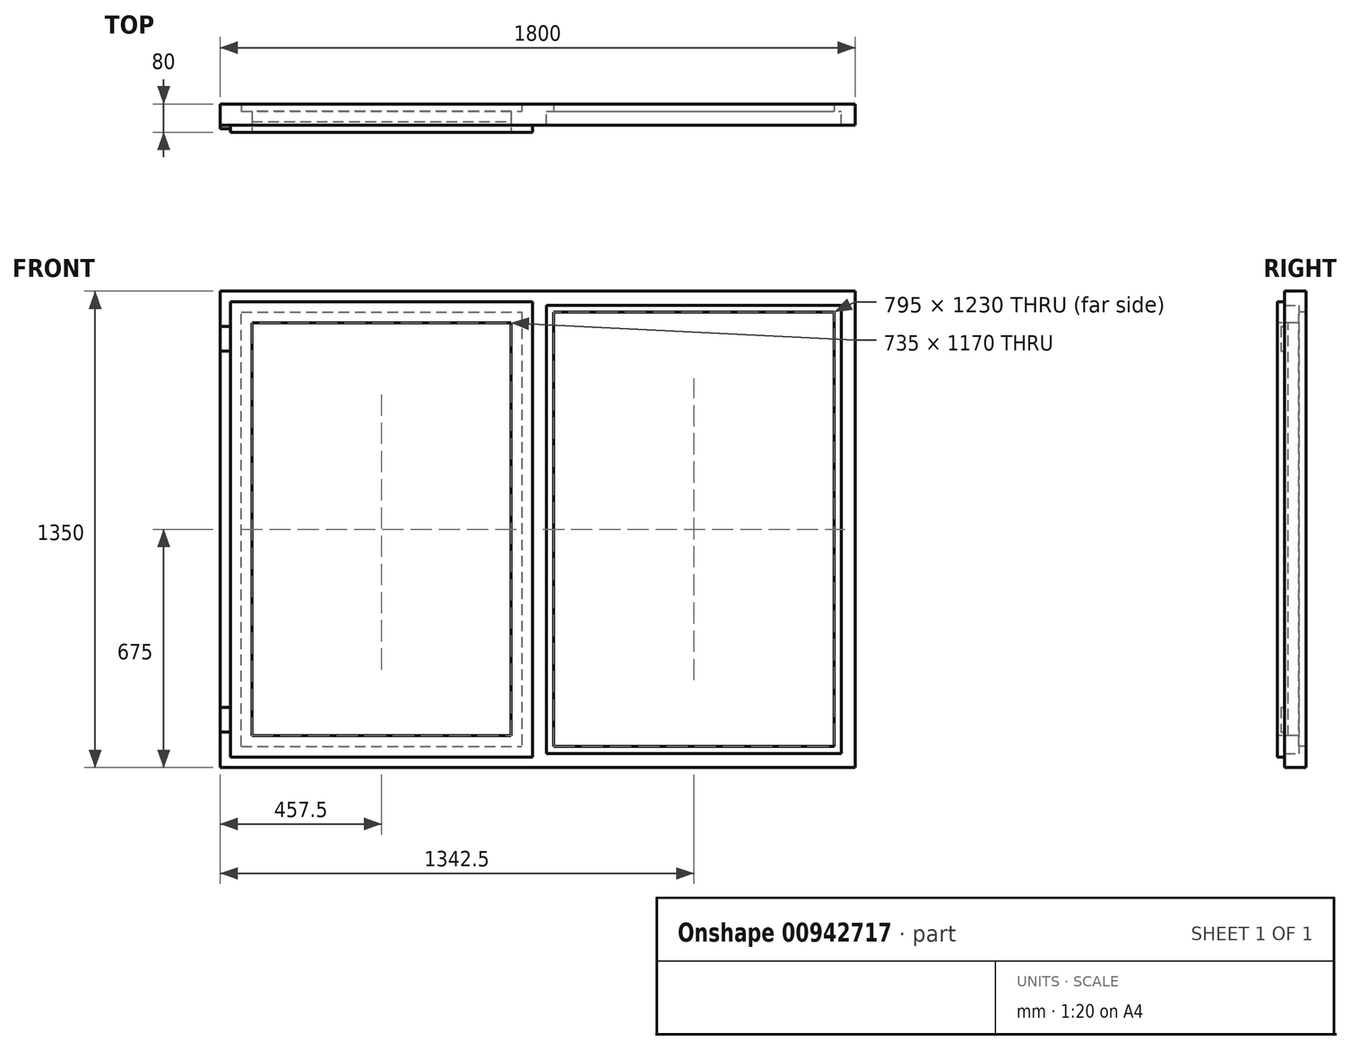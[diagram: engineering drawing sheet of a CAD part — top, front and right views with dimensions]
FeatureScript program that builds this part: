
annotation { "Feature Type Name" : "Feature", "Feature Type Description" : "" }
export const myFeature = defineFeature(function(context is Context, id is Id, definition is map)
    precondition{}
    {
        {
            var Q0;
            Q0=qCreatedBy(makeId("Front.planeOp"),FACE);
            var sketch = newSketch(context, id + "F0", { "sketchPlane" : qUnion([Q0])});
            skLineSegment(sketch, "E0.bottom", {"start": v(900, 675) * mm, "end": v(-900, 675) * mm});
            skLineSegment(sketch, "E0.top", {"start": v(900, -675) * mm, "end": v(-900, -675) * mm});
            skLineSegment(sketch, "E0.left", {"start": v(900, 675) * mm, "end": v(900, -675) * mm});
            skLineSegment(sketch, "E0.right", {"start": v(-900, 675) * mm, "end": v(-900, -675) * mm});
            skLineSegment(sketch, "E1", {"start": v(0, 675) * mm, "end": v(0, 0) * mm, "construction": true});
            skLineSegment(sketch, "E2", {"start": v(900, 0) * mm, "end": v(0, 0) * mm, "construction": true});
            skLineSegment(sketch, "E3", {"start": v(0, 0) * mm, "end": v(-900, 0) * mm, "construction": true});
            skLineSegment(sketch, "E4.bottom", {"start": v(-860, 635) * mm, "end": v(860, 635) * mm});
            skLineSegment(sketch, "E4.top", {"start": v(-860, -635) * mm, "end": v(860, -635) * mm});
            skLineSegment(sketch, "E4.left", {"start": v(-860, 635) * mm, "end": v(-860, -635) * mm});
            skLineSegment(sketch, "E4.right", {"start": v(860, 635) * mm, "end": v(860, -635) * mm});
            skLineSegment(sketch, "E5", {"start": v(0, 0) * mm, "end": v(0, -635) * mm, "construction": true});
            skLineSegment(sketch, "E6", {"start": v(0, 635) * mm, "end": v(0, -635) * mm, "construction": true});
            skLineSegment(sketch, "E7.bottom", {"start": v(-840, -615) * mm, "end": v(840, -615) * mm});
            skLineSegment(sketch, "E7.top", {"start": v(-840, 615) * mm, "end": v(840, 615) * mm});
            skLineSegment(sketch, "E7.left", {"start": v(-840, -615) * mm, "end": v(-840, 615) * mm});
            skLineSegment(sketch, "E7.right", {"start": v(840, -615) * mm, "end": v(840, 615) * mm});
            skLineSegment(sketch, "E8", {"start": v(-25, 635) * mm, "end": v(-25, -635) * mm});
            skLineSegment(sketch, "E9", {"start": v(25, -635) * mm, "end": v(25, 635) * mm});
            skLineSegment(sketch, "E10", {"start": v(-45, 615) * mm, "end": v(-45, -615) * mm});
            skLineSegment(sketch, "E11", {"start": v(45, -615) * mm, "end": v(45, 615) * mm});
            skSolve(sketch);
        }
        {
            var Q0;
            Q0=makeQuery(id+"F0.imprint","IMPRINT",FACE,{"disambiguationData":[TD([[makeQuery(id+"F0.imprint","IMPRINT",EDGE,{"derivedFrom":sQuery(id+"F0.wireOp",EDGE,"E0.bottom")}),1.0]])]});
            extrude(context, id + "F1", {"entities" : qUnion([Q0]), "depth" : 40 * mm, "offsetDistance" : 25 * mm});
        }
        {
            var Q0;
            {var subQ0=sQuery(id+"F0.wireOp",EDGE,"E4.left");Q0=makeQuery(id+"F0.imprint","IMPRINT",FACE,{"disambiguationData":[TD([[makeQuery(id+"F0.imprint","IMPRINT",EDGE,{"derivedFrom":subQ0}),1.0]])]});}
            var Q1;
            {var subQ8=sQuery(id+"F0.wireOp",EDGE,"E4.right");Q1=makeQuery(id+"F0.imprint","IMPRINT",FACE,{"disambiguationData":[TD([[makeQuery(id+"F0.imprint","IMPRINT",EDGE,{"derivedFrom":subQ8}),-1.0]])]});}
            var Q2;
            {var subQ0=sQuery(id+"F0.wireOp",EDGE,"E8");var subQ1=sQuery(id+"F0.wireOp",EDGE,"E4.top");var subQ2=makeQuery(id+"F0.imprint","INTERSECT",VERTEX,{"derivedFrom":[subQ1,subQ0]});Q2=makeQuery(id+"F0.imprint","IMPRINT",FACE,{"disambiguationData":[TD([[makeQuery(id+"F0.imprint","IMPRINT",EDGE,{"disambiguationData":[TD([[subQ2,-1.0]])],"derivedFrom":subQ1}),1.0]])]});}
            var Q3;
            {var subQ0=sQuery(id+"F0.wireOp",EDGE,"E8");var subQ1=sQuery(id+"F0.wireOp",EDGE,"E4.bottom");var subQ2=makeQuery(id+"F0.imprint","INTERSECT",VERTEX,{"derivedFrom":[subQ1,subQ0]});Q3=makeQuery(id+"F0.imprint","IMPRINT",FACE,{"disambiguationData":[TD([[makeQuery(id+"F0.imprint","IMPRINT",EDGE,{"disambiguationData":[TD([[subQ2,-1.0]])],"derivedFrom":subQ1}),-1.0]])]});}
            var Q4;
            Q4=makeQuery(id+"F0.imprint","IMPRINT",FACE,{"disambiguationData":[TD([[makeQuery(id+"F0.imprint","IMPRINT",EDGE,{"derivedFrom":sQuery(id+"F0.wireOp",EDGE,"E0.bottom")}),1.0]])]});
            var Q5;
            {var subQ0=sQuery(id+"F0.wireOp",EDGE,"E11");Q5=makeQuery(id+"F0.imprint","IMPRINT",FACE,{"disambiguationData":[TD([[makeQuery(id+"F0.imprint","IMPRINT",EDGE,{"derivedFrom":subQ0}),1.0]])]});}
            var Q6;
            {var subQ0=sQuery(id+"F0.wireOp",EDGE,"E10");Q6=makeQuery(id+"F0.imprint","IMPRINT",FACE,{"disambiguationData":[TD([[makeQuery(id+"F0.imprint","IMPRINT",EDGE,{"derivedFrom":subQ0}),1.0]])]});}
            var Q7;
            {var subQ0=sQuery(id+"F0.wireOp",EDGE,"E8");var subQ1=sQuery(id+"F0.wireOp",EDGE,"E7.bottom");var subQ2=makeQuery(id+"F0.imprint","INTERSECT",VERTEX,{"derivedFrom":[subQ1,subQ0]});Q7=makeQuery(id+"F0.imprint","IMPRINT",FACE,{"disambiguationData":[TD([[makeQuery(id+"F0.imprint","IMPRINT",EDGE,{"disambiguationData":[TD([[subQ2,-1.0]])],"derivedFrom":subQ1}),1.0]])]});}
            extrude(context, id + "F2", {"entities" : qUnion([Q0, Q1, Q2, Q3, Q4, Q5, Q6, Q7]), "operationType" : NewBodyOperationType.ADD, "oppositeDirection" : true, "depth" : 20 * mm, "offsetDistance" : 25 * mm});
        }
        {
            var Q0;
            {var subQ0=sQuery(id+"F0.wireOp",EDGE,"E8");var subQ1=sQuery(id+"F0.wireOp",EDGE,"E7.bottom");var subQ2=makeQuery(id+"F0.imprint","INTERSECT",VERTEX,{"derivedFrom":[subQ1,subQ0]});Q0=makeQuery(id+"F0.imprint","IMPRINT",FACE,{"disambiguationData":[TD([[makeQuery(id+"F0.imprint","IMPRINT",EDGE,{"disambiguationData":[TD([[subQ2,-1.0]])],"derivedFrom":subQ1}),1.0]])]});}
            var Q1;
            {var subQ0=sQuery(id+"F0.wireOp",EDGE,"E8");var subQ1=sQuery(id+"F0.wireOp",EDGE,"E4.bottom");var subQ2=makeQuery(id+"F0.imprint","INTERSECT",VERTEX,{"derivedFrom":[subQ1,subQ0]});Q1=makeQuery(id+"F0.imprint","IMPRINT",FACE,{"disambiguationData":[TD([[makeQuery(id+"F0.imprint","IMPRINT",EDGE,{"disambiguationData":[TD([[subQ2,-1.0]])],"derivedFrom":subQ1}),-1.0]])]});}
            var Q2;
            {var subQ0=sQuery(id+"F0.wireOp",EDGE,"E8");var subQ1=sQuery(id+"F0.wireOp",EDGE,"E4.top");var subQ2=makeQuery(id+"F0.imprint","INTERSECT",VERTEX,{"derivedFrom":[subQ1,subQ0]});Q2=makeQuery(id+"F0.imprint","IMPRINT",FACE,{"disambiguationData":[TD([[makeQuery(id+"F0.imprint","IMPRINT",EDGE,{"disambiguationData":[TD([[subQ2,-1.0]])],"derivedFrom":subQ1}),1.0]])]});}
            extrude(context, id + "F3", {"entities" : qUnion([Q0, Q1, Q2]), "operationType" : NewBodyOperationType.ADD, "depth" : 40 * mm, "offsetDistance" : 25 * mm, "hasSecondDirection" : true, "secondDirectionOppositeDirection" : true, "secondDirectionDepth" : 20 * mm});
        }
        {
            var Q0;
            {var subQ0=sQuery(id+"F0.wireOp",EDGE,"E4.top");var subQ1=sQuery(id+"F0.wireOp",EDGE,"E4.bottom");Q0=makeQuery(id+"F3.boolean.opBoolean","MERGE",FACE,{"derivedFrom":[makeQuery(id+"F1.opExtrude","CAP_FACE",FACE,{"disambiguationData":[OSD([sQuery(id+"F0.wireOp",EDGE,"E0.bottom"),sQuery(id+"F0.wireOp",EDGE,"E0.top"),sQuery(id+"F0.wireOp",EDGE,"E0.left"),sQuery(id+"F0.wireOp",EDGE,"E0.right"),subQ1,subQ0,sQuery(id+"F0.wireOp",EDGE,"E4.left"),sQuery(id+"F0.wireOp",EDGE,"E4.right")])],"isStart":false}),makeQuery(id+"F3.opExtrude","CAP_FACE",FACE,{"disambiguationData":[OSD([subQ1,subQ0,sQuery(id+"F0.wireOp",EDGE,"E8"),sQuery(id+"F0.wireOp",EDGE,"E9")])],"isStart":false})]});}
            var sketch = newSketch(context, id + "F4", { "sketchPlane" : qUnion([Q0])});
            skLineSegment(sketch, "E12.bottom", {"start": v(-860, 635) * mm, "end": v(-25, 635) * mm});
            skLineSegment(sketch, "E12.top", {"start": v(-860, -635) * mm, "end": v(-25, -635) * mm});
            skLineSegment(sketch, "E12.left", {"start": v(-860, 635) * mm, "end": v(-860, -635) * mm});
            skLineSegment(sketch, "E12.right", {"start": v(-25, 635) * mm, "end": v(-25, -635) * mm});
            skLineSegment(sketch, "E13.bottom", {"start": v(-870, -645) * mm, "end": v(-15, -645) * mm});
            skLineSegment(sketch, "E13.top", {"start": v(-870, 645) * mm, "end": v(-15, 645) * mm});
            skLineSegment(sketch, "E13.left", {"start": v(-870, -645) * mm, "end": v(-870, 645) * mm});
            skLineSegment(sketch, "E13.right", {"start": v(-15, -645) * mm, "end": v(-15, 645) * mm});
            skLineSegment(sketch, "E14.bottom", {"start": v(-810, -585) * mm, "end": v(-75, -585) * mm});
            skLineSegment(sketch, "E14.top", {"start": v(-810, 585) * mm, "end": v(-75, 585) * mm});
            skLineSegment(sketch, "E14.left", {"start": v(-810, -585) * mm, "end": v(-810, 585) * mm});
            skLineSegment(sketch, "E14.right", {"start": v(-75, -585) * mm, "end": v(-75, 585) * mm});
            skLineSegment(sketch, "E15.bottom", {"start": v(-870, 575) * mm, "end": v(-900, 575) * mm});
            skLineSegment(sketch, "E15.top", {"start": v(-870, 505) * mm, "end": v(-900, 505) * mm});
            skLineSegment(sketch, "E15.left", {"start": v(-870, 575) * mm, "end": v(-870, 505) * mm});
            skLineSegment(sketch, "E15.right", {"start": v(-900, 575) * mm, "end": v(-900, 505) * mm});
            skLineSegment(sketch, "E16.bottom", {"start": v(-870, -575) * mm, "end": v(-900, -575) * mm});
            skLineSegment(sketch, "E16.top", {"start": v(-870, -505) * mm, "end": v(-900, -505) * mm});
            skLineSegment(sketch, "E16.left", {"start": v(-870, -575) * mm, "end": v(-870, -505) * mm});
            skLineSegment(sketch, "E16.right", {"start": v(-900, -575) * mm, "end": v(-900, -505) * mm});
            skSolve(sketch);
        }
        {
            var Q0;
            Q0=makeQuery(id+"F4.imprint","IMPRINT",FACE,{"disambiguationData":[TD([[makeQuery(id+"F4.imprint","IMPRINT",EDGE,{"derivedFrom":sQuery(id+"F4.wireOp",EDGE,"E12.bottom")}),-1.0]])]});
            var Q1;
            {var subQ0=sQuery(id+"F0.wireOp",EDGE,"E7.left");var subQ1=sQuery(id+"F0.wireOp",EDGE,"E7.bottom");var subQ2=sQuery(id+"F0.wireOp",EDGE,"E10");var subQ3=sQuery(id+"F0.wireOp",EDGE,"E7.top");Q1=makeQuery(id+"F3.boolean.opBoolean","SPLIT",FACE,{"disambiguationData":[TD([makeQuery(id+"F1.opExtrude","SWEPT_FACE",FACE,{"disambiguationData":[OSD([sQuery(id+"F0.wireOp",EDGE,"E4.left")])]})])],"derivedFrom":makeQuery(id+"F2.opExtrude","CAP_FACE",FACE,{"disambiguationData":[OSD([sQuery(id+"F0.wireOp",EDGE,"E0.bottom"),sQuery(id+"F0.wireOp",EDGE,"E0.top"),sQuery(id+"F0.wireOp",EDGE,"E0.left"),sQuery(id+"F0.wireOp",EDGE,"E0.right"),subQ1,subQ3,subQ0,sQuery(id+"F0.wireOp",EDGE,"E7.right"),subQ2,sQuery(id+"F0.wireOp",EDGE,"E11")])],"isStart":true})});}
            extrude(context, id + "F5", {"entities" : qUnion([Q0]), "endBound" : BoundingType.UP_TO_SURFACE, "oppositeDirection" : true, "depth" : 25 * mm, "endBoundEntityFace" : qUnion([Q1]), "offsetDistance" : 25 * mm});
        }
        {
            var Q0;
            Q0=makeQuery(id+"F4.imprint","IMPRINT",FACE,{"disambiguationData":[TD([[makeQuery(id+"F4.imprint","IMPRINT",EDGE,{"derivedFrom":sQuery(id+"F4.wireOp",EDGE,"E12.bottom")}),-1.0]])]});
            var Q1;
            Q1=makeQuery(id+"F4.imprint","IMPRINT",FACE,{"disambiguationData":[TD([[makeQuery(id+"F4.imprint","IMPRINT",EDGE,{"derivedFrom":sQuery(id+"F4.wireOp",EDGE,"E12.bottom")}),1.0]])]});
            extrude(context, id + "F6", {"entities" : qUnion([Q0, Q1]), "operationType" : NewBodyOperationType.ADD, "depth" : 20 * mm, "offsetDistance" : 25 * mm});
        }
        {
            var Q0;
            Q0=makeQuery(id+"F4.imprint","IMPRINT",FACE,{"disambiguationData":[TD([[makeQuery(id+"F4.imprint","IMPRINT",EDGE,{"derivedFrom":sQuery(id+"F4.wireOp",EDGE,"E14.bottom")}),1.0]])]});
            extrude(context, id + "F7", {"entities" : qUnion([Q0]), "oppositeDirection" : true, "depth" : 10 * mm, "offsetDistance" : 25 * mm});
        }
        {
            var Q0;
            Q0=makeQuery(id+"F4.imprint","IMPRINT",FACE,{"disambiguationData":[TD([[makeQuery(id+"F4.imprint","IMPRINT",EDGE,{"derivedFrom":sQuery(id+"F4.wireOp",EDGE,"E15.bottom")}),1.0]])]});
            var Q1;
            Q1=makeQuery(id+"F4.imprint","IMPRINT",FACE,{"disambiguationData":[TD([[makeQuery(id+"F4.imprint","IMPRINT",EDGE,{"derivedFrom":sQuery(id+"F4.wireOp",EDGE,"E16.bottom")}),-1.0]])]});
            extrude(context, id + "F8", {"entities" : qUnion([Q0, Q1]), "operationType" : NewBodyOperationType.ADD, "depth" : 10 * mm, "offsetDistance" : 25 * mm});
        }
    });
